# Revit family: Sanitary_Showers_hansgrohe_26842700-Rainfinity-Showerpipe
name_source: partatom
category: Plumbing Fixtures
units: mm (PartAtom-declared; Revit-internal decimal feet)

## family parameters
Always vertical = No
Cut with Voids When Loaded = No
OmniClass Number = 23.45.00.00
OmniClass Title = Sanitary, Laundry, and Cleaning Equipment
Part Type = Normal
Room Calculation Point = No
Round Connector Dimension = Use Diameter
Shared = No
Work Plane-Based = Yes

## types (1)
- Matt White
    BIMobject category = Showers
    BIMobject category code = sanitary-showers
    BIMobject main category = Sanitary
    BIMobject main category code = sanitary
    BOSUseNativeGeometries = 1
    Brand url = http://www.hansgrohe-int.com
    Default Elevation = 4' - 0"
    Edition number = 1
    IFC Classification = Sanitary Terminal
    Installation instructions = https://pro.hansgrohe-int.com
    Manufacturer country = Germany
    Manufacturer name = hansgrohe
    Masterformat 2014 Code = 22 41 23
    Masterformat 2014 Description = Residential Showers
    NBS Reference Code = 35-06-81
    NBS Reference Description = Shower Heads
    OmniClass Code = 23-31 17 19
    OmniClass Description = Shower Head Fixtures
    Product Guid = a08e3216-5c47-499d-b5d2-a3d5c569f05e
    Product SKU = 26842700
    Product data url = https://bimobject.com
    Product family = Rainfinity
    Product group = Showerpipes universal
    Product name = 26842700 Rainfinity Showerpipe 360 1jet for concealed installation 26842700
    Product url = https://pro.hansgrohe-int.com
    QR code = http://bimobject.com
    Technical description = https://pro.hansgrohe-int.com
    UNSPSC Code = 30181503
    Uniclass 1.4 Code = L7214
    Uniclass 1.4 Description = Showers
    Uniclass 2.0 Code = PR-35-06-81
    Uniclass 2.0 Description = Shower Heads
    Uniclass 2015 Code = Pr_40_20_87_76
    Uniclass 2015 Name = Shower heads
    Uniformat II Code = D2090
    Uniformat II Description = Other Plumbing Systems

## geometry (parser evidence)
native form markers: Sweep x4
no freeform markers — native parametric forms only
